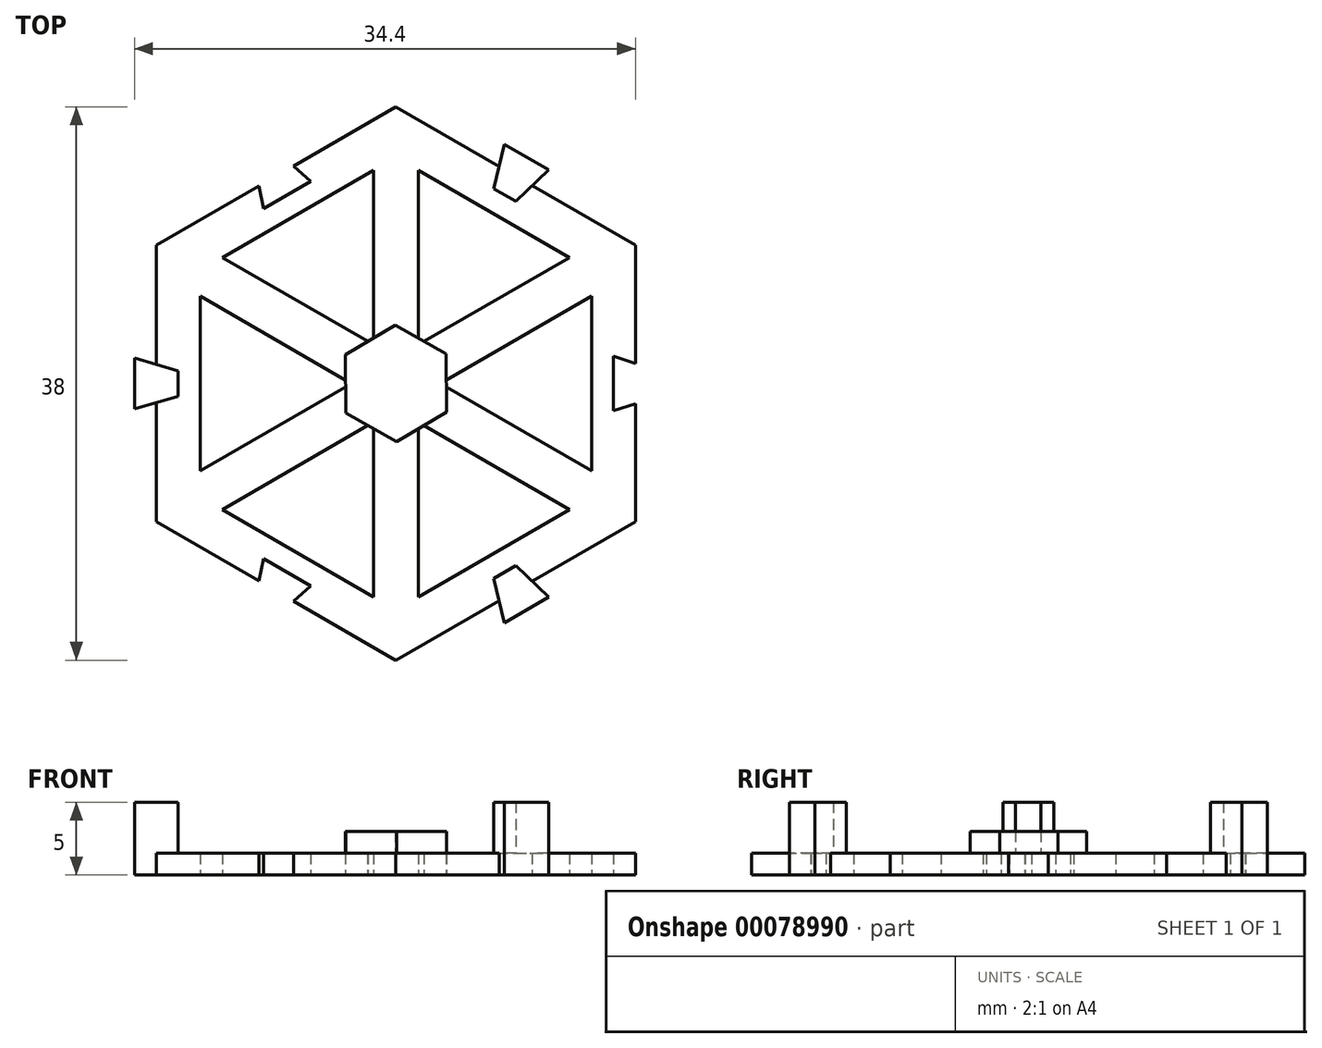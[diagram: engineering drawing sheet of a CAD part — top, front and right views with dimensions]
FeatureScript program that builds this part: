
annotation { "Feature Type Name" : "Feature", "Feature Type Description" : "" }
export const myFeature = defineFeature(function(context is Context, id is Id, definition is map)
    precondition{}
    {
        {
            var Q0;
            Q0=qCreatedBy(makeId("Top.planeOp"),FACE);
            var sketch = newSketch(context, id + "F0", { "sketchPlane" : qUnion([Q0])});
            skCircle(sketch, "E0.cCircle", {"center": v(0, 0) * mm, "radius": 16.45 * mm, "construction": true});
            skLineSegment(sketch, "E0.0", {"start": v(16.45, 9.5) * mm, "end": v(16.45, -9.5) * mm});
            skLineSegment(sketch, "E0.1", {"start": v(16.45, -9.5) * mm, "end": v(0, -19) * mm});
            skLineSegment(sketch, "E0.2", {"start": v(0, -19) * mm, "end": v(-16.45, -9.5) * mm});
            skLineSegment(sketch, "E0.3", {"start": v(-16.45, -9.5) * mm, "end": v(-16.45, 9.5) * mm});
            skLineSegment(sketch, "E0.4", {"start": v(-16.45, 9.5) * mm, "end": v(0, 19) * mm});
            skLineSegment(sketch, "E0.5", {"start": v(0, 19) * mm, "end": v(16.45, 9.5) * mm});
            skPoint(sketch, "E0.0.midPoint", {"position": v(16.45, 0) * mm});
            skPoint(sketch, "E1.0.midPoint", {"position": v(5.66, 0) * mm});
            skLineSegment(sketch, "E2", {"start": v(0, 0) * mm, "end": v(0, 19) * mm});
            skLineSegment(sketch, "E3", {"start": v(0, 0) * mm, "end": v(16.45, 9.5) * mm});
            skLineSegment(sketch, "E4", {"start": v(0, 0) * mm, "end": v(16.45, -9.5) * mm});
            skLineSegment(sketch, "E5", {"start": v(0, 0) * mm, "end": v(0, -19) * mm});
            skLineSegment(sketch, "E6", {"start": v(0, 0) * mm, "end": v(-16.45, -9.5) * mm});
            skLineSegment(sketch, "E7", {"start": v(0, 0) * mm, "end": v(-16.45, 9.5) * mm});
            skCircle(sketch, "E8.cCircle", {"center": v(0, 0) * mm, "radius": 4.78 * mm, "construction": true});
            skLineSegment(sketch, "E8.0", {"start": v(0, 5.52) * mm, "end": v(4.78, 2.76) * mm});
            skLineSegment(sketch, "E8.1", {"start": v(4.78, 2.76) * mm, "end": v(4.78, -2.76) * mm});
            skLineSegment(sketch, "E8.2", {"start": v(4.78, -2.76) * mm, "end": v(0, -5.52) * mm});
            skLineSegment(sketch, "E8.3", {"start": v(0, -5.52) * mm, "end": v(-4.78, -2.76) * mm});
            skLineSegment(sketch, "E8.4", {"start": v(-4.78, -2.76) * mm, "end": v(-4.78, 2.76) * mm});
            skLineSegment(sketch, "E8.5", {"start": v(-4.78, 2.76) * mm, "end": v(0, 5.52) * mm});
            skPoint(sketch, "E8.0.midPoint", {"position": v(2.4, 4.14) * mm});
            skLineSegment(sketch, "E9", {"start": v(0, 0) * mm, "end": v(8.23, 14.25) * mm, "construction": true});
            skLineSegment(sketch, "E10.0", {"start": v(-11.92, 8.65) * mm, "end": v(-1.53, 14.65) * mm});
            skLineSegment(sketch, "E10.1", {"start": v(-1.53, 2.65) * mm, "end": v(-11.92, 8.65) * mm});
            skLineSegment(sketch, "E10.2", {"start": v(-1.53, 2.65) * mm, "end": v(-1.53, 14.65) * mm});
            skLineSegment(sketch, "E11.bottom", {"start": v(-9.74, 13.38) * mm, "end": v(-6.71, 15.13) * mm});
            skLineSegment(sketch, "E11.top", {"start": v(-9.1, 12.01) * mm, "end": v(-5.85, 13.89) * mm});
            skLineSegment(sketch, "E12", {"start": v(0, 0) * mm, "end": v(-7.48, 12.95) * mm, "construction": true});
            skLineSegment(sketch, "E13", {"start": v(16.45, 0) * mm, "end": v(-16.45, 0) * mm, "construction": true});
            skLineSegment(sketch, "E14", {"start": v(-9.74, 15.11) * mm, "end": v(-8.22, 15.99) * mm});
            skLineSegment(sketch, "E15", {"start": v(-9.74, 15.11) * mm, "end": v(-9.1, 12.01) * mm});
            skLineSegment(sketch, "E16", {"start": v(-8.22, 15.99) * mm, "end": v(-5.85, 13.89) * mm});
            skLineSegment(sketch, "E17", {"start": v(-8.23, 14.25) * mm, "end": v(-8.98, 15.55) * mm});
            skLineSegment(sketch, "E18.MirrorCS", {"start": v(1.53, -14.65) * mm, "end": v(11.92, -8.65) * mm});
            skLineSegment(sketch, "E19.MirrorCS", {"start": v(1.53, -2.65) * mm, "end": v(11.92, -8.65) * mm});
            skLineSegment(sketch, "E20.MirrorCS", {"start": v(1.53, -2.65) * mm, "end": v(1.53, -14.65) * mm});
            skLineSegment(sketch, "E21.MirrorCS", {"start": v(0, 0) * mm, "end": v(7.48, -12.95) * mm, "construction": true});
            skLineSegment(sketch, "E22.MirrorCS", {"start": v(6.72, -13.39) * mm, "end": v(8.24, -12.51) * mm});
            skLineSegment(sketch, "E23.MirrorCS", {"start": v(7.46, -16.42) * mm, "end": v(10.5, -14.67) * mm});
            skLineSegment(sketch, "E24.MirrorCS", {"start": v(6.72, -13.39) * mm, "end": v(7.46, -16.42) * mm});
            skLineSegment(sketch, "E25.MirrorCS", {"start": v(8.24, -12.51) * mm, "end": v(10.5, -14.67) * mm});
            skLineSegment(sketch, "E26.MirrorCS", {"start": v(8.24, 12.51) * mm, "end": v(10.5, 14.67) * mm});
            skLineSegment(sketch, "E27.MirrorCS", {"start": v(7.46, 16.42) * mm, "end": v(10.5, 14.67) * mm});
            skLineSegment(sketch, "E28.MirrorCS", {"start": v(6.72, 13.39) * mm, "end": v(7.46, 16.42) * mm});
            skLineSegment(sketch, "E29.MirrorCS", {"start": v(6.72, 13.39) * mm, "end": v(8.24, 12.51) * mm});
            skLineSegment(sketch, "E30.MirrorCS", {"start": v(1.53, 2.65) * mm, "end": v(11.92, 8.65) * mm});
            skLineSegment(sketch, "E31.MirrorCS", {"start": v(1.53, 14.65) * mm, "end": v(11.92, 8.65) * mm});
            skLineSegment(sketch, "E32.MirrorCS", {"start": v(1.53, 2.65) * mm, "end": v(1.53, 14.65) * mm});
            skLineSegment(sketch, "E33.0", {"start": v(8.19, 12.9) * mm, "end": v(9.99, 14.61) * mm});
            skLineSegment(sketch, "E33.1", {"start": v(7.07, 13.54) * mm, "end": v(8.19, 12.9) * mm});
            skLineSegment(sketch, "E33.2", {"start": v(7.07, 13.54) * mm, "end": v(7.66, 15.96) * mm});
            skLineSegment(sketch, "E33.3", {"start": v(7.66, 15.96) * mm, "end": v(9.99, 14.61) * mm});
            skLineSegment(sketch, "E34", {"start": v(0, 0) * mm, "end": v(-6.73, 11.65) * mm, "construction": true});
            skSolve(sketch);
        }
        {
            var Q0;
            {var subQ4=sQuery(id+"F0.wireOp",EDGE,"E8.0");Q0=makeQuery(id+"F0.imprint","IMPRINT",FACE,{"disambiguationData":[TD([[makeQuery(id+"F0.imprint","IMPRINT",EDGE,{"derivedFrom":subQ4}),1.0]])]});}
            var Q1;
            {var subQ3=sQuery(id+"F0.wireOp",EDGE,"E8.0");Q1=makeQuery(id+"F0.imprint","IMPRINT",FACE,{"disambiguationData":[TD([[makeQuery(id+"F0.imprint","IMPRINT",EDGE,{"derivedFrom":subQ3}),-1.0]])]});}
            var Q2;
            {var subQ3=sQuery(id+"F0.wireOp",EDGE,"E8.5");Q2=makeQuery(id+"F0.imprint","IMPRINT",FACE,{"disambiguationData":[TD([[makeQuery(id+"F0.imprint","IMPRINT",EDGE,{"derivedFrom":subQ3}),-1.0]])]});}
            var Q3;
            {var subQ5=sQuery(id+"F0.wireOp",EDGE,"E8.5");Q3=makeQuery(id+"F0.imprint","IMPRINT",FACE,{"disambiguationData":[TD([[makeQuery(id+"F0.imprint","IMPRINT",EDGE,{"derivedFrom":subQ5}),1.0]])]});}
            extrude(context, id + "F1", {"entities" : qUnion([Q0, Q1, Q2, Q3]), "depth" : 1.5 * mm});
        }
        {
            var Q0;
            {var subQ0=sQuery(id+"F0.wireOp",EDGE,"E29.MirrorCS");Q0=makeQuery(id+"F0.imprint","IMPRINT",FACE,{"disambiguationData":[TD([[makeQuery(id+"F0.imprint","IMPRINT",EDGE,{"derivedFrom":subQ0}),1.0]])]});}
            var Q1;
            {var subQ5=sQuery(id+"F0.wireOp",EDGE,"E33.1");Q1=makeQuery(id+"F0.imprint","IMPRINT",FACE,{"disambiguationData":[TD([[makeQuery(id+"F0.imprint","IMPRINT",EDGE,{"derivedFrom":subQ5}),1.0]])]});}
            var Q2;
            {var subQ5=sQuery(id+"F0.wireOp",EDGE,"E33.3");Q2=makeQuery(id+"F0.imprint","IMPRINT",FACE,{"disambiguationData":[TD([[makeQuery(id+"F0.imprint","IMPRINT",EDGE,{"derivedFrom":subQ5}),-1.0]])]});}
            var Q3;
            {var subQ0=sQuery(id+"F0.wireOp",EDGE,"E27.MirrorCS");Q3=makeQuery(id+"F0.imprint","IMPRINT",FACE,{"disambiguationData":[TD([[makeQuery(id+"F0.imprint","IMPRINT",EDGE,{"derivedFrom":subQ0}),-1.0]])]});}
            extrude(context, id + "F2", {"entities" : qUnion([Q0, Q1, Q2, Q3]), "operationType" : NewBodyOperationType.ADD, "depth" : 5 * mm});
        }
        {
            var Q0;
            Q0=makeQuery(id+"F1.opExtrude","SWEPT_BODY",BODY,{"disambiguationData":[OSD([sQuery(id+"F0.wireOp",EDGE,"E0.4"),sQuery(id+"F0.wireOp",EDGE,"E0.5"),sQuery(id+"F0.wireOp",EDGE,"E3"),sQuery(id+"F0.wireOp",EDGE,"E7"),sQuery(id+"F0.wireOp",EDGE,"E10.0"),sQuery(id+"F0.wireOp",EDGE,"E10.1"),sQuery(id+"F0.wireOp",EDGE,"E10.2"),sQuery(id+"F0.wireOp",EDGE,"E11.bottom"),sQuery(id+"F0.wireOp",EDGE,"E11.top"),sQuery(id+"F0.wireOp",EDGE,"E15"),sQuery(id+"F0.wireOp",EDGE,"E16"),sQuery(id+"F0.wireOp",EDGE,"E26.MirrorCS"),sQuery(id+"F0.wireOp",EDGE,"E28.MirrorCS"),sQuery(id+"F0.wireOp",EDGE,"E29.MirrorCS"),sQuery(id+"F0.wireOp",EDGE,"E30.MirrorCS"),sQuery(id+"F0.wireOp",EDGE,"E31.MirrorCS"),sQuery(id+"F0.wireOp",EDGE,"E32.MirrorCS")])]});
            var Q1;
            Q1=makeQuery(id+"F1.opExtrude","SWEPT_EDGE",EDGE,{"disambiguationData":[OSD([sQuery(id+"F0.wireOp",EDGE,"E2"),sQuery(id+"F0.wireOp",EDGE,"E3"),sQuery(id+"F0.wireOp",EDGE,"E4"),sQuery(id+"F0.wireOp",EDGE,"E5"),sQuery(id+"F0.wireOp",EDGE,"E6"),sQuery(id+"F0.wireOp",EDGE,"E7")])]});
            transform(context, id + "F3", {"entities" : qUnion([Q0]), "transformType" : TransformType.ROTATION, "transformAxis" : qUnion([Q1]), "angle" : 120 * degree, "makeCopy" : true});
        }
        {
            var Q0;
            Q0=makeQuery(id+"F3.opPattern","COPY",BODY,{"derivedFrom":makeQuery(id+"F1.opExtrude","SWEPT_BODY",BODY,{"disambiguationData":[OSD([sQuery(id+"F0.wireOp",EDGE,"E0.4"),sQuery(id+"F0.wireOp",EDGE,"E0.5"),sQuery(id+"F0.wireOp",EDGE,"E3"),sQuery(id+"F0.wireOp",EDGE,"E7"),sQuery(id+"F0.wireOp",EDGE,"E10.0"),sQuery(id+"F0.wireOp",EDGE,"E10.1"),sQuery(id+"F0.wireOp",EDGE,"E10.2"),sQuery(id+"F0.wireOp",EDGE,"E11.bottom"),sQuery(id+"F0.wireOp",EDGE,"E11.top"),sQuery(id+"F0.wireOp",EDGE,"E15"),sQuery(id+"F0.wireOp",EDGE,"E16"),sQuery(id+"F0.wireOp",EDGE,"E26.MirrorCS"),sQuery(id+"F0.wireOp",EDGE,"E28.MirrorCS"),sQuery(id+"F0.wireOp",EDGE,"E29.MirrorCS"),sQuery(id+"F0.wireOp",EDGE,"E30.MirrorCS"),sQuery(id+"F0.wireOp",EDGE,"E31.MirrorCS"),sQuery(id+"F0.wireOp",EDGE,"E32.MirrorCS")])]}),"instanceName":"1"});
            var Q1;
            Q1=makeQuery(id+"F1.opExtrude","SWEPT_EDGE",EDGE,{"disambiguationData":[OSD([sQuery(id+"F0.wireOp",EDGE,"E2"),sQuery(id+"F0.wireOp",EDGE,"E3"),sQuery(id+"F0.wireOp",EDGE,"E4"),sQuery(id+"F0.wireOp",EDGE,"E5"),sQuery(id+"F0.wireOp",EDGE,"E6"),sQuery(id+"F0.wireOp",EDGE,"E7")])]});
            transform(context, id + "F4", {"entities" : qUnion([Q0]), "transformType" : TransformType.ROTATION, "transformAxis" : qUnion([Q1]), "angle" : 120 * degree, "makeCopy" : true});
        }
        {
            var Q0;
            Q0=qCreatedBy(makeId("Top.planeOp"),FACE);
            var sketch = newSketch(context, id + "F5", { "sketchPlane" : qUnion([Q0])});
            skCircle(sketch, "E35.cCircle", {"center": v(0, 0) * mm, "radius": 3.46 * mm, "construction": true});
            skLineSegment(sketch, "E35.0", {"start": v(3.48, -1.97) * mm, "end": v(0.04, -4) * mm});
            skLineSegment(sketch, "E35.1", {"start": v(0.04, -4) * mm, "end": v(-3.45, -2.03) * mm});
            skLineSegment(sketch, "E35.2", {"start": v(-3.45, -2.03) * mm, "end": v(-3.48, 1.97) * mm});
            skLineSegment(sketch, "E35.3", {"start": v(-3.48, 1.97) * mm, "end": v(-0.04, 4) * mm});
            skLineSegment(sketch, "E35.4", {"start": v(-0.04, 4) * mm, "end": v(3.45, 2.03) * mm});
            skLineSegment(sketch, "E35.5", {"start": v(3.45, 2.03) * mm, "end": v(3.48, -1.97) * mm});
            skPoint(sketch, "E35.0.midPoint", {"position": v(1.76, -2.98) * mm});
            skSolve(sketch);
        }
        {
            var Q0;
            Q0=makeQuery(id+"F5.imprint","IMPRINT",FACE,{"disambiguationData":[TD([[makeQuery(id+"F5.imprint","IMPRINT",EDGE,{"derivedFrom":sQuery(id+"F5.wireOp",EDGE,"E35.0")}),-1.0]])]});
            extrude(context, id + "F6", {"entities" : qUnion([Q0]), "operationType" : NewBodyOperationType.ADD, "depth" : 3 * mm});
        }
    });
